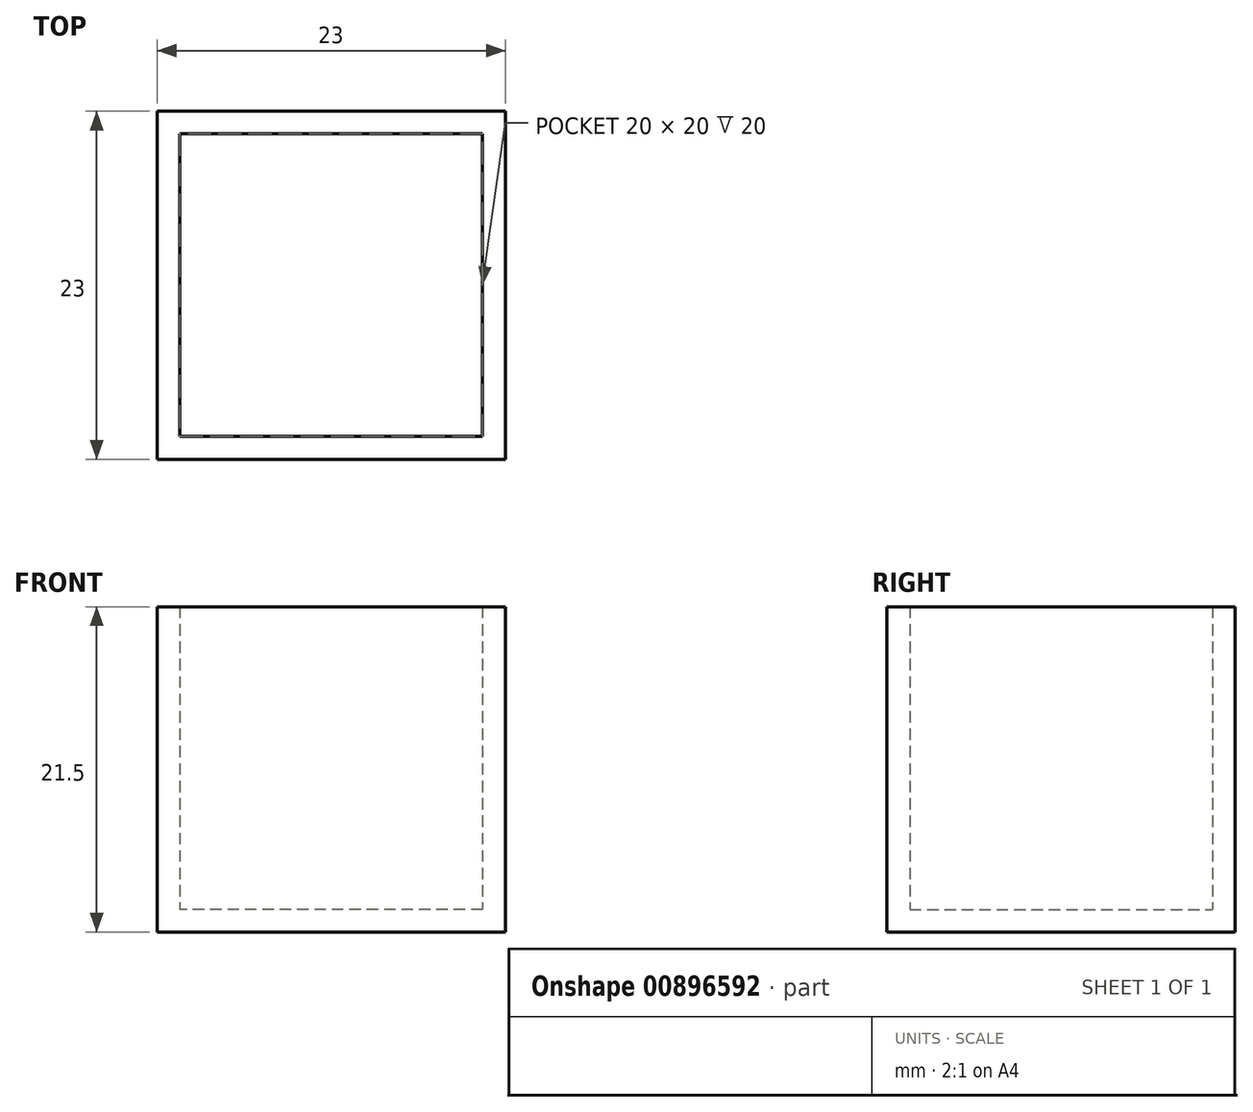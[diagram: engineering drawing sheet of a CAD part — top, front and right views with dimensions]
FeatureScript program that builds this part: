
annotation { "Feature Type Name" : "Feature", "Feature Type Description" : "" }
export const myFeature = defineFeature(function(context is Context, id is Id, definition is map)
    precondition{}
    {
        {
            var Q0;
            Q0=qCreatedBy(makeId("Top.planeOp"),FACE);
            var sketch = newSketch(context, id + "F0", { "sketchPlane" : qUnion([Q0])});
            skLineSegment(sketch, "E0.bottom", {"start": v(10, -10) * mm, "end": v(-10, -10) * mm});
            skLineSegment(sketch, "E0.top", {"start": v(10, 10) * mm, "end": v(-10, 10) * mm});
            skLineSegment(sketch, "E0.left", {"start": v(10, -10) * mm, "end": v(10, 10) * mm});
            skLineSegment(sketch, "E0.right", {"start": v(-10, -10) * mm, "end": v(-10, 10) * mm});
            skPoint(sketch, "E0.middle", {"position": v(0, 0) * mm});
            skLineSegment(sketch, "E1.0", {"start": v(11.5, 11.5) * mm, "end": v(-11.5, 11.5) * mm});
            skLineSegment(sketch, "E1.1", {"start": v(11.5, -11.5) * mm, "end": v(11.5, 11.5) * mm});
            skLineSegment(sketch, "E1.2", {"start": v(11.5, -11.5) * mm, "end": v(-11.5, -11.5) * mm});
            skLineSegment(sketch, "E1.3", {"start": v(-11.5, -11.5) * mm, "end": v(-11.5, 11.5) * mm});
            skSolve(sketch);
        }
        {
            var Q0;
            Q0 = qSketchRegion(id + "F0", true);
            var Q1;
            Q1=makeQuery(id+"F0.imprint","IMPRINT",FACE,{"disambiguationData":[TD([[makeQuery(id+"F0.imprint","IMPRINT",EDGE,{"derivedFrom":sQuery(id+"F0.wireOp",EDGE,"E0.bottom")}),-1.0]])]});
            extrude(context, id + "F1", {"entities" : qUnion([Q0, Q1]), "oppositeDirection" : true, "depth" : 1.5 * mm, "offsetDistance" : 25 * mm});
        }
        {
            var Q0;
            Q0 = qSketchRegion(id + "F0", true);
            extrude(context, id + "F2", {"entities" : qUnion([Q0]), "operationType" : NewBodyOperationType.ADD, "depth" : 20 * mm, "offsetDistance" : 25 * mm});
        }
    });
